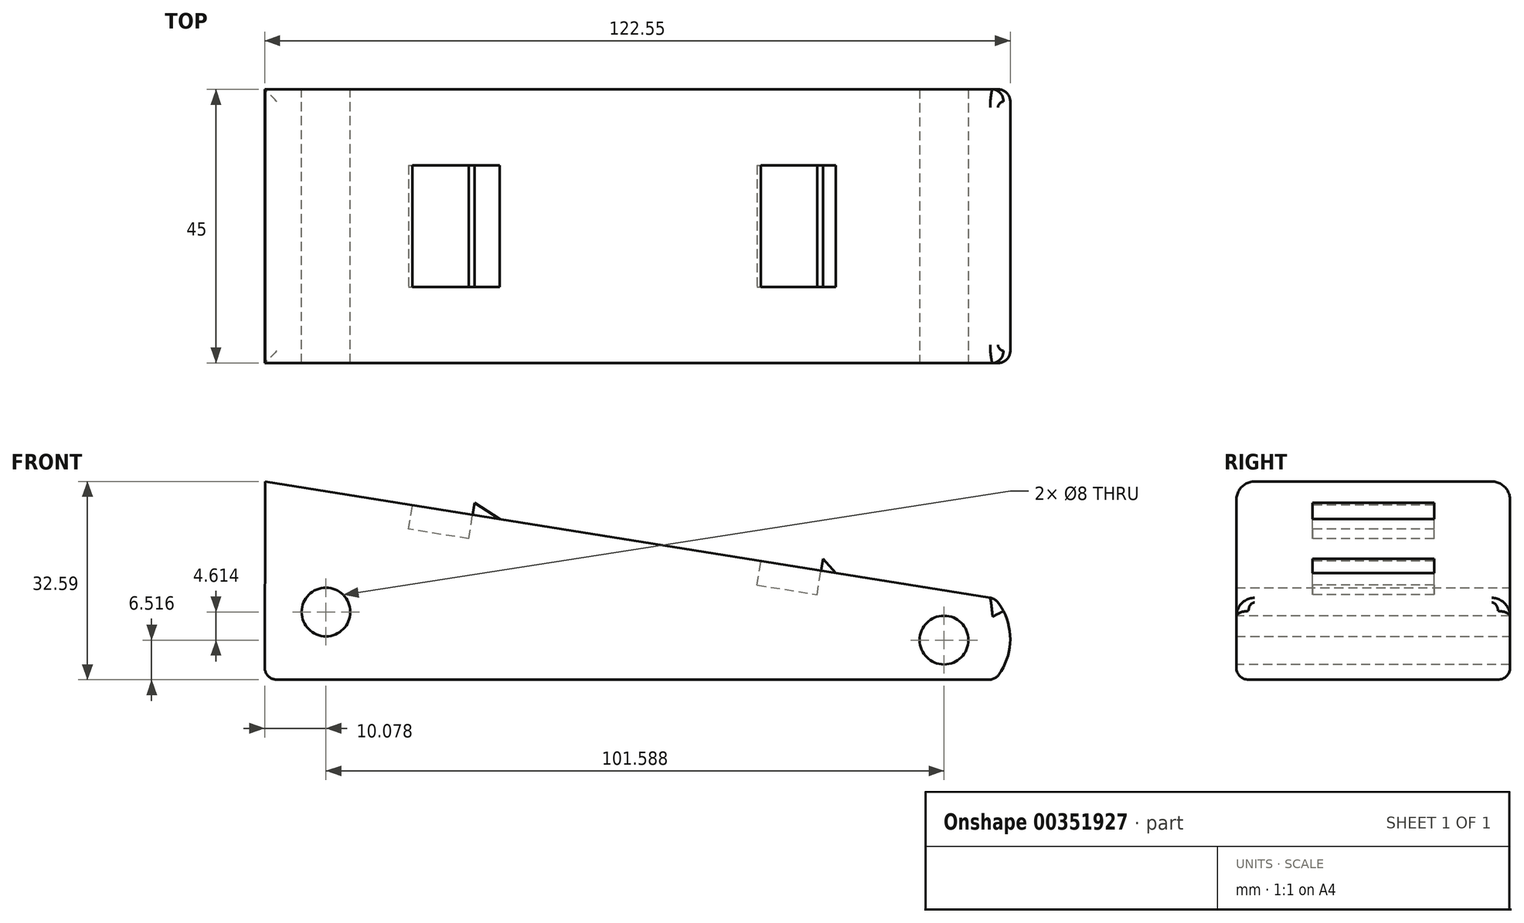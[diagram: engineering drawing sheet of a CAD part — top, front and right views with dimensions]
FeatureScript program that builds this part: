
annotation { "Feature Type Name" : "Feature", "Feature Type Description" : "" }
export const myFeature = defineFeature(function(context is Context, id is Id, definition is map)
    precondition{}
    {
        {
            var Q0;
            Q0=qCreatedBy(makeId("Front.planeOp"),FACE);
            var sketch = newSketch(context, id + "F0", { "sketchPlane" : qUnion([Q0])});
            skPoint(sketch, "E0.endSnap0", {"position": v(0, 6.96) * mm});
            skArc(sketch, "E1", {"start": v(0, 0) * mm, "mid": v(2.55, 6.67) * mm, "end": v(0, 13.35) * mm});
            skLineSegment(sketch, "E2", {"start": v(-120, 0) * mm, "end": v(0, 0) * mm});
            skLineSegment(sketch, "E3", {"start": v(-119.92, 32.6) * mm, "end": v(0, 13.35) * mm});
            skPoint(sketch, "E4.orphan", {"position": v(-119.92, 43.9) * mm});
            skLineSegment(sketch, "E5", {"start": v(-120, 0) * mm, "end": v(-119.92, 32.6) * mm});
            skSolve(sketch);
        }
        {
            var Q0;
            Q0 = qSketchRegion(id + "F0", true);
            extrude(context, id + "F1", {"entities" : qUnion([Q0]), "depth" : 45 * mm});
        }
        {
            var Q0;
            Q0=makeQuery(id+"F1.opExtrude","CAP_EDGE",EDGE,{"disambiguationData":[OSD([sQuery(id+"F0.wireOp",EDGE,"E2")])],"isStart":false});
            var Q1;
            Q1=makeQuery(id+"F1.opExtrude","CAP_EDGE",EDGE,{"disambiguationData":[OSD([sQuery(id+"F0.wireOp",EDGE,"E2")])],"isStart":true});
            var Q2;
            Q2=makeQuery(id+"F1.opExtrude","SWEPT_EDGE",EDGE,{"disambiguationData":[OSD([sQuery(id+"F0.wireOp",EDGE,"E1"),sQuery(id+"F0.wireOp",EDGE,"E2")])]});
            var Q3;
            Q3=makeQuery(id+"F1.opExtrude","SWEPT_EDGE",EDGE,{"disambiguationData":[OSD([sQuery(id+"F0.wireOp",EDGE,"N2XC1PoU-3hC8-9kNy-WHY7-5EFzRKXKMXRw"),sQuery(id+"F0.wireOp",EDGE,"E1")])]});
            var Q4;
            Q4=makeQuery(id+"F1.opExtrude","CAP_EDGE",EDGE,{"disambiguationData":[OSD([sQuery(id+"F0.wireOp",EDGE,"N2XC1PoU-3hC8-9kNy-WHY7-5EFzRKXKMXRw")])],"isStart":false});
            var Q5;
            Q5=makeQuery(id+"F1.opExtrude","CAP_EDGE",EDGE,{"disambiguationData":[OSD([sQuery(id+"F0.wireOp",EDGE,"N2XC1PoU-3hC8-9kNy-WHY7-5EFzRKXKMXRw")])],"isStart":true});
            var Q6;
            Q6=makeQuery(id+"F1.opExtrude","SWEPT_EDGE",EDGE,{"disambiguationData":[OSD([sQuery(id+"F0.wireOp",EDGE,"GJ5NP7sF-dkZj-9cmc-kMZy-r74nJc1zXekC"),sQuery(id+"F0.wireOp",EDGE,"E2")])]});
            var Q7;
            Q7=makeQuery(id+"F1.opExtrude","CAP_EDGE",EDGE,{"disambiguationData":[OSD([sQuery(id+"F0.wireOp",EDGE,"E1")])],"isStart":false});
            var Q8;
            Q8=makeQuery(id+"F1.opExtrude","CAP_EDGE",EDGE,{"disambiguationData":[OSD([sQuery(id+"F0.wireOp",EDGE,"E1")])],"isStart":true});
            fillet(context, id + "F2", {"entities" : qUnion([Q0, Q1, Q2, Q3, Q4, Q5, Q6, Q7, Q8]), "radius" : 2 * mm, "tangentPropagation" : true, "allowEdgeOverflow" : false});
        }
        {
            var Q0;
            Q0=makeQuery(id+"F1.opExtrude","CAP_FACE",FACE,{"disambiguationData":[OSD([sQuery(id+"F0.wireOp",EDGE,"38iJ4YLK-JbyQ-QrXa-Neti-xotfABrVJHRt"),sQuery(id+"F0.wireOp",EDGE,"N2XC1PoU-3hC8-9kNy-WHY7-5EFzRKXKMXRw"),sQuery(id+"F0.wireOp",EDGE,"E1"),sQuery(id+"F0.wireOp",EDGE,"aQqyr7ku-gGe9-KPt3-KeBI-ATJ6dId1f1QY"),sQuery(id+"F0.wireOp",EDGE,"GJ5NP7sF-dkZj-9cmc-kMZy-r74nJc1zXekC"),sQuery(id+"F0.wireOp",EDGE,"E2")])],"isStart":false});
            var sketch = newSketch(context, id + "F3", { "sketchPlane" : qUnion([Q0])});
            skCircle(sketch, "E6", {"center": v(-109.92, 11.13) * mm, "radius": 3.5 * mm});
            skCircle(sketch, "E7", {"center": v(-8.33, 6.52) * mm, "radius": 3.5 * mm});
            skLineSegment(sketch, "E8", {"start": v(-4.33, 14.04) * mm, "end": v(-4.33, 2) * mm});
            skLineSegment(sketch, "E9", {"start": v(-4.33, 2) * mm, "end": v(-4.33, 8.02) * mm});
            skLineSegment(sketch, "E10", {"start": v(-4.33, 2) * mm, "end": v(-4.33, 5.01) * mm});
            skLineSegment(sketch, "E11", {"start": v(-4.33, 5.01) * mm, "end": v(-4.33, 8.02) * mm});
            skLineSegment(sketch, "E12", {"start": v(-4.33, 6.52) * mm, "end": v(-4.33, 8.02) * mm});
            skLineSegment(sketch, "E13", {"start": v(-4.33, 6.52) * mm, "end": v(-8.33, 6.52) * mm});
            skSolve(sketch);
        }
        {
            var Q0;
            Q0=makeQuery(id+"F1.opExtrude","CAP_FACE",FACE,{"disambiguationData":[OSD([sQuery(id+"F0.wireOp",EDGE,"38iJ4YLK-JbyQ-QrXa-Neti-xotfABrVJHRt"),sQuery(id+"F0.wireOp",EDGE,"N2XC1PoU-3hC8-9kNy-WHY7-5EFzRKXKMXRw"),sQuery(id+"F0.wireOp",EDGE,"E1"),sQuery(id+"F0.wireOp",EDGE,"aQqyr7ku-gGe9-KPt3-KeBI-ATJ6dId1f1QY"),sQuery(id+"F0.wireOp",EDGE,"GJ5NP7sF-dkZj-9cmc-kMZy-r74nJc1zXekC"),sQuery(id+"F0.wireOp",EDGE,"E2")])],"isStart":true});
            var sketch = newSketch(context, id + "F4", { "sketchPlane" : qUnion([Q0])});
            skCircle(sketch, "E14", {"center": v(109.92, 11.13) * mm, "radius": 2.5 * mm});
            skPoint(sketch, "E15", {"position": v(4.94, 6.2) * mm});
            skCircle(sketch, "E16", {"center": v(4.94, 6.2) * mm, "radius": 2.5 * mm});
            skSolve(sketch);
        }
        {
            var Q0;
            Q0=sQuery(id+"F4.wireOp",VERTEX,"E14.center");
            var Q1;
            Q1=makeQuery(id+"F1.opExtrude","SWEPT_BODY",BODY,{"disambiguationData":[OSD([sQuery(id+"F0.wireOp",EDGE,"38iJ4YLK-JbyQ-QrXa-Neti-xotfABrVJHRt"),sQuery(id+"F0.wireOp",EDGE,"N2XC1PoU-3hC8-9kNy-WHY7-5EFzRKXKMXRw"),sQuery(id+"F0.wireOp",EDGE,"E1"),sQuery(id+"F0.wireOp",EDGE,"aQqyr7ku-gGe9-KPt3-KeBI-ATJ6dId1f1QY"),sQuery(id+"F0.wireOp",EDGE,"GJ5NP7sF-dkZj-9cmc-kMZy-r74nJc1zXekC"),sQuery(id+"F0.wireOp",EDGE,"E2")])]});
            hole(context, id + "F5", {"style" : HoleStyle.SIMPLE, "endStyle" : HoleEndStyle.THROUGH, "holeDiameter" : 8 * mm, "isTappedThrough" : true, "tappedDepth" : 12 * mm, "tapClearance" : 3, "locations" : qUnion([Q0]), "scope" : qUnion([Q1])});
        }
        {
            var Q0;
            Q0=sQuery(id+"F3.wireOp",VERTEX,"E7.center");
            var Q1;
            Q1=makeQuery(id+"F1.opExtrude","SWEPT_BODY",BODY,{"disambiguationData":[OSD([sQuery(id+"F0.wireOp",EDGE,"38iJ4YLK-JbyQ-QrXa-Neti-xotfABrVJHRt"),sQuery(id+"F0.wireOp",EDGE,"N2XC1PoU-3hC8-9kNy-WHY7-5EFzRKXKMXRw"),sQuery(id+"F0.wireOp",EDGE,"E1"),sQuery(id+"F0.wireOp",EDGE,"aQqyr7ku-gGe9-KPt3-KeBI-ATJ6dId1f1QY"),sQuery(id+"F0.wireOp",EDGE,"GJ5NP7sF-dkZj-9cmc-kMZy-r74nJc1zXekC"),sQuery(id+"F0.wireOp",EDGE,"E2")])]});
            hole(context, id + "F6", {"style" : HoleStyle.SIMPLE, "endStyle" : HoleEndStyle.THROUGH, "holeDiameter" : 8 * mm, "isTappedThrough" : true, "tappedDepth" : 12 * mm, "tapClearance" : 3, "locations" : qUnion([Q0]), "scope" : qUnion([Q1])});
        }
        {
            var Q0;
            Q0=makeQuery(id+"F1.opExtrude","SWEPT_FACE",FACE,{"disambiguationData":[OSD([sQuery(id+"F0.wireOp",EDGE,"E3")])]});
            var sketch = newSketch(context, id + "F7", { "sketchPlane" : qUnion([Q0])});
            skLineSegment(sketch, "E17", {"start": v(-65.04, 0) * mm, "end": v(-89.04, 0) * mm});
            skLineSegment(sketch, "E18", {"start": v(-89.04, -22.5) * mm, "end": v(-89.04, -32.5) * mm});
            skLineSegment(sketch, "E19", {"start": v(-89.04, -22.5) * mm, "end": v(-89.04, -12.5) * mm});
            skLineSegment(sketch, "E20", {"start": v(-89.04, -12.5) * mm, "end": v(-99.04, -12.5) * mm});
            skLineSegment(sketch, "E21", {"start": v(-99.04, -12.5) * mm, "end": v(-99.04, -32.5) * mm});
            skLineSegment(sketch, "E22", {"start": v(-99.04, -32.5) * mm, "end": v(-89.04, -32.5) * mm});
            skLineSegment(sketch, "E23", {"start": v(-65.04, 0) * mm, "end": v(-41.04, 0) * mm});
            skLineSegment(sketch, "E24.bottom", {"start": v(-41.04, -12.5) * mm, "end": v(-31.04, -12.5) * mm});
            skLineSegment(sketch, "E24.top", {"start": v(-41.04, -32.5) * mm, "end": v(-31.04, -32.5) * mm});
            skLineSegment(sketch, "E24.right", {"start": v(-31.04, -12.5) * mm, "end": v(-31.04, -32.5) * mm});
            skLineSegment(sketch, "E25", {"start": v(-41.04, -12.5) * mm, "end": v(-41.04, -32.5) * mm});
            skSolve(sketch);
        }
        {
            var Q0;
            Q0=makeQuery(id+"F1.opExtrude","CAP_EDGE",EDGE,{"disambiguationData":[OSD([sQuery(id+"F0.wireOp",EDGE,"E3")])],"isStart":true});
            var Q1;
            Q1=makeQuery(id+"F1.opExtrude","CAP_EDGE",EDGE,{"disambiguationData":[OSD([sQuery(id+"F0.wireOp",EDGE,"E3")])],"isStart":false});
            fillet(context, id + "F8", {"entities" : qUnion([Q0, Q1]), "radius" : 3 * mm, "tangentPropagation" : true, "allowEdgeOverflow" : false});
        }
        {
            var Q0;
            Q0 = qSketchRegion(id + "F7", true);
            extrude(context, id + "F9", {"entities" : qUnion([Q0]), "operationType" : NewBodyOperationType.REMOVE, "oppositeDirection" : true, "depth" : 4 * mm});
        }
        {
            var Q0;
            Q0=makeQuery(id+"F1.opExtrude","SWEPT_FACE",FACE,{"disambiguationData":[OSD([sQuery(id+"F0.wireOp",EDGE,"E3")])]});
            var sketch = newSketch(context, id + "F10", { "sketchPlane" : qUnion([Q0])});
            skLineSegment(sketch, "E26.bottom", {"start": v(-89.04, -32.5) * mm, "end": v(-84.54, -32.5) * mm});
            skLineSegment(sketch, "E26.top", {"start": v(-89.04, -12.5) * mm, "end": v(-84.54, -12.5) * mm});
            skLineSegment(sketch, "E26.left", {"start": v(-89.04, -32.5) * mm, "end": v(-89.04, -12.5) * mm});
            skLineSegment(sketch, "E26.right", {"start": v(-84.54, -32.5) * mm, "end": v(-84.54, -12.5) * mm});
            skLineSegment(sketch, "E27.bottom", {"start": v(-31.04, -32.5) * mm, "end": v(-28.54, -32.5) * mm});
            skLineSegment(sketch, "E27.top", {"start": v(-31.04, -12.5) * mm, "end": v(-28.54, -12.5) * mm});
            skLineSegment(sketch, "E27.left", {"start": v(-31.04, -32.5) * mm, "end": v(-31.04, -12.5) * mm});
            skLineSegment(sketch, "E27.right", {"start": v(-28.54, -32.5) * mm, "end": v(-28.54, -12.5) * mm});
            skSolve(sketch);
        }
        {
            var Q0;
            Q0 = qSketchRegion(id + "F10", true);
            extrude(context, id + "F11", {"entities" : qUnion([Q0]), "operationType" : NewBodyOperationType.ADD, "depth" : 2 * mm});
        }
        {
            var Q0;
            Q0=makeQuery(id+"F11.opExtrude","CAP_EDGE",EDGE,{"disambiguationData":[OSD([sQuery(id+"F10.wireOp",EDGE,"E26.right")])],"isStart":false});
            chamfer(context, id + "F12", {"entities" : qUnion([Q0]), "chamferType" : ChamferType.OFFSET_ANGLE, "width" : 4.5 * mm, "oppositeDirection" : false, "angle" : 24 * degree, "tangentPropagation" : true});
        }
        {
            var Q0;
            Q0=makeQuery(id+"F11.opExtrude","CAP_EDGE",EDGE,{"disambiguationData":[OSD([sQuery(id+"F10.wireOp",EDGE,"E27.right")])],"isStart":false});
            chamfer(context, id + "F13", {"entities" : qUnion([Q0]), "chamferType" : ChamferType.OFFSET_ANGLE, "width" : 2.45 * mm, "oppositeDirection" : false, "angle" : 40 * degree, "tangentPropagation" : true});
        }
    });
